# Revit family: 205_SIL-50-_-300
name_source: partatom
category: Duct Accessories
units: mm (PartAtom-declared; Revit-internal decimal feet)

## family parameters
Always vertical = Yes
Cut with Voids When Loaded = No
Part Type = Breaks Into
Round Connector Dimension = Use Diameter
Shared = No
Work Plane-Based = No

## types (6) — shared parameters
Description = CIRCULAR SILENCER
L2D = 300 mm
LL = 150 mm  [stored 0.492126 ft]
Manufacturer = Alnor
QmdConnectorList = 201;D;202;D
URL = http://www.ventilation-alnor.co.uk
magiPartTypeId = 205
magiProductFamilyId = SIL-50-*-300

## per-type parameters (varying)
| type | CD1 | CD2 | D | H2D | L1 | L2 | R | SW1 | W2D |
| SIL-50-080-300 | 90 mm  [stored 0.295276 ft] | 91 mm  [stored 0.298556 ft] | 80 mm | 180 mm  [stored 0.590551 ft] | 4 mm  [stored 0.0131234 ft] | 292 mm  [stored 0.958005 ft] | 40 mm  [stored 0.131234 ft] | Yes | 180 mm  [stored 0.590551 ft] |
| SIL-50-200-300 | 150 mm  [stored 0.492126 ft] | 151 mm | 200 mm | 300 mm | 36 mm | 228 mm | 100 mm  [stored 0.328084 ft] | No | 300 mm |
| SIL-50-160-300 | 125 mm | 126 mm | 160 mm | 260 mm | 36 mm | 228 mm | 80 mm  [stored 0.262467 ft] | No | 260 mm |
| SIL-50-150-300 | 125 mm | 126 mm | 150 mm | 250 mm | 4 mm  [stored 0.0131234 ft] | 292 mm  [stored 0.958005 ft] | 75 mm  [stored 0.246063 ft] | Yes | 250 mm |
| SIL-50-125-300 | 112 mm | 113 mm | 125 mm | 225 mm | 36 mm | 228 mm | 63 mm | No | 225 mm |
| SIL-50-100-300 | 100 mm  [stored 0.328084 ft] | 101 mm | 100 mm | 200 mm | 36 mm | 228 mm | 50 mm | No | 200 mm |

note: column(s) folded — value = type name in every type: MC Product Code, magiProductId

note: [stored X ft] marks values corroborated as IEEE doubles in the binary element streams (Revit-internal decimal feet)

## geometry (parser evidence)
native form markers: Blend x4, Sweep x1
no freeform markers — native parametric forms only
